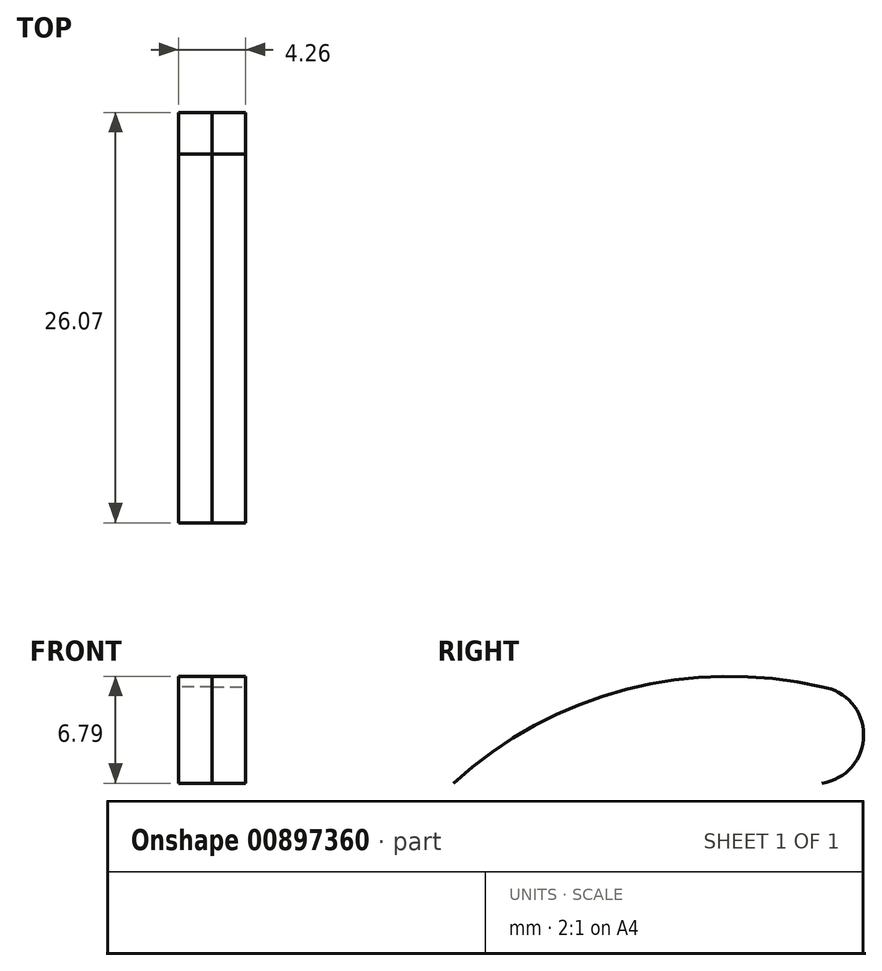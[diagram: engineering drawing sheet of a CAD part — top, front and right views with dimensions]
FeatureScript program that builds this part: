
annotation { "Feature Type Name" : "Feature", "Feature Type Description" : "" }
export const myFeature = defineFeature(function(context is Context, id is Id, definition is map)
    precondition{}
    {
        {
            var Q0;
            Q0=qCreatedBy(makeId("Top.planeOp"),FACE);
            var sketch = newSketch(context, id + "F0", { "sketchPlane" : qUnion([Q0])});
            skLineSegment(sketch, "E0.bottom", {"start": v(19.08, 37.88) * mm, "end": v(-19.08, 37.88) * mm});
            skLineSegment(sketch, "E0.top", {"start": v(6.36, -37.88) * mm, "end": v(-6.36, -37.88) * mm});
            skLineSegment(sketch, "E0.left", {"start": v(25.4, 26.45) * mm, "end": v(25.4, -18.34) * mm});
            skLineSegment(sketch, "E0.right", {"start": v(-25.4, 26.45) * mm, "end": v(-25.4, -18.34) * mm});
            skPoint(sketch, "E0.middle", {"position": v(0, 0) * mm});
            skArc(sketch, "E1", {"start": v(-6.36, -37.88) * mm, "mid": v(-13.5, -25.8) * mm, "end": v(-25.4, -18.34) * mm});
            skArc(sketch, "E2", {"start": v(25.4, -18.34) * mm, "mid": v(13.5, -25.8) * mm, "end": v(6.36, -37.88) * mm});
            skPoint(sketch, "E3.orphan", {"position": v(-25.4, -37.88) * mm});
            skPoint(sketch, "E4.orphan", {"position": v(25.4, -37.88) * mm});
            skLineSegment(sketch, "E5.top", {"start": v(-25.4, 26.45) * mm, "end": v(-19.08, 26.45) * mm});
            skLineSegment(sketch, "E5.right", {"start": v(-19.08, 37.88) * mm, "end": v(-19.08, 26.45) * mm});
            skLineSegment(sketch, "E6.top", {"start": v(25.4, 26.45) * mm, "end": v(19.08, 26.45) * mm});
            skLineSegment(sketch, "E6.right", {"start": v(19.08, 37.88) * mm, "end": v(19.08, 26.45) * mm});
            skPoint(sketch, "E5.bottom.start.orphan", {"position": v(-25.4, 37.88) * mm});
            skPoint(sketch, "E7.orphan", {"position": v(25.4, 37.88) * mm});
            skLineSegment(sketch, "E8.bottom", {"start": v(22.4, -58.7) * mm, "end": v(-22.4, -58.7) * mm});
            skLineSegment(sketch, "E8.top", {"start": v(22.4, -53.16) * mm, "end": v(-22.4, -53.16) * mm});
            skLineSegment(sketch, "E8.left", {"start": v(22.4, -58.7) * mm, "end": v(22.4, -53.16) * mm});
            skLineSegment(sketch, "E8.right", {"start": v(-22.4, -58.7) * mm, "end": v(-22.4, -53.16) * mm});
            skPoint(sketch, "E8.middle", {"position": v(0, -55.93) * mm});
            skSolve(sketch);
        }
        {
            var Q0;
            Q0=qCreatedBy(makeId("Right.planeOp"),FACE);
            var sketch = newSketch(context, id + "F1", { "sketchPlane" : qUnion([Q0])});
            skArc(sketch, "E9", {"start": v(-32.5, 0) * mm, "mid": v(-29.86, 3.06) * mm, "end": v(-32.5, 6.12) * mm});
            skArc(sketch, "E10", {"start": v(-32.5, 6.12) * mm, "mid": v(-44.97, 5.94) * mm, "end": v(-55.93, 0) * mm});
            skLineSegment(sketch, "E11", {"start": v(-32.5, 0) * mm, "end": v(-32.5, 6.12) * mm, "construction": true});
            skPoint(sketch, "E12", {"position": v(-32.5, 0) * mm});
            skSolve(sketch);
        }
        {
            var Q0;
            Q0 = qSketchRegion(id + "F1", true);
            var Q1;
            Q1=sQuery(id+"F1.wireOp",EDGE,"E10");
            var Q2;
            Q2=sQuery(id+"F1.wireOp",EDGE,"E9");
            extrude(context, id + "F2", {"entities" : qUnion([Q0]), "bodyType" : ToolBodyType.SURFACE, "surfaceEntities" : qUnion([Q1, Q2]), "depth" : 2.13 * mm, "offsetDistance" : 25.4 * mm});
        }
        {
            var Q0;
            Q0=makeQuery(id+"F2.opExtrude","SWEPT_BODY",BODY,{"disambiguationData":[OSD([sQuery(id+"F1.wireOp",EDGE,"E9")])]});
            var Q1;
            Q1=qCreatedBy(makeId("Right.planeOp"),FACE);
            mirror(context, id + "F3", {"entities" : qUnion([Q0]), "mirrorPlane" : qUnion([Q1])});
        }
    });
